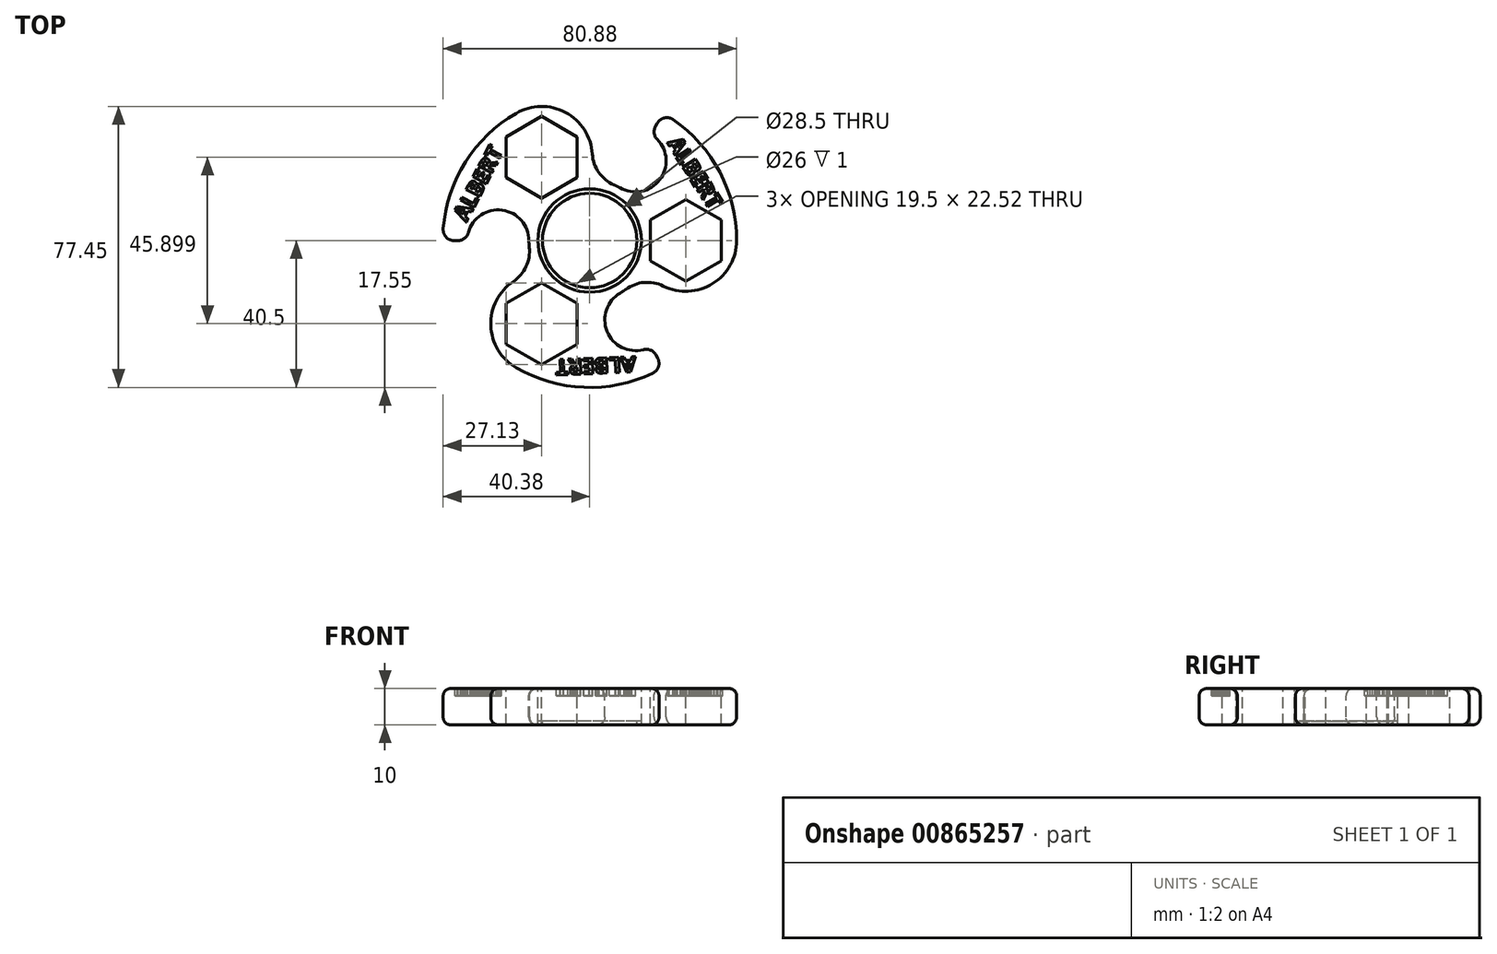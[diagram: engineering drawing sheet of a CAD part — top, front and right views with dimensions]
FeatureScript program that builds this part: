
annotation { "Feature Type Name" : "Feature", "Feature Type Description" : "" }
export const myFeature = defineFeature(function(context is Context, id is Id, definition is map)
    precondition{}
    {
        {
            var Q0;
            Q0=qCreatedBy(makeId("Top.planeOp"),FACE);
            var sketch = newSketch(context, id + "F0", { "sketchPlane" : qUnion([Q0])});
            skCircle(sketch, "E0", {"center": v(0, 0) * mm, "radius": 14.25 * mm});
            skCircle(sketch, "E1.cCircle", {"center": v(26.5, 0) * mm, "radius": 9.75 * mm, "construction": true});
            skLineSegment(sketch, "E1.0", {"start": v(36.25, 5.63) * mm, "end": v(36.25, -5.63) * mm});
            skLineSegment(sketch, "E1.1", {"start": v(36.25, -5.63) * mm, "end": v(26.5, -11.26) * mm});
            skLineSegment(sketch, "E1.2", {"start": v(26.5, -11.26) * mm, "end": v(16.75, -5.63) * mm});
            skLineSegment(sketch, "E1.3", {"start": v(16.75, -5.63) * mm, "end": v(16.75, 5.63) * mm});
            skLineSegment(sketch, "E1.4", {"start": v(16.75, 5.63) * mm, "end": v(26.5, 11.26) * mm});
            skLineSegment(sketch, "E1.5", {"start": v(26.5, 11.26) * mm, "end": v(36.25, 5.63) * mm});
            skPoint(sketch, "E1.0.midPoint", {"position": v(9.75, 0) * mm});
            skLineSegment(sketch, "E2", {"start": v(26.5, 11.26) * mm, "end": v(16.75, 5.63) * mm});
            skLineSegment(sketch, "E3", {"start": v(16.75, 5.63) * mm, "end": v(16.75, -5.63) * mm});
            skLineSegment(sketch, "E4", {"start": v(16.75, -5.63) * mm, "end": v(26.5, -11.26) * mm});
            skLineSegment(sketch, "E5", {"start": v(26.5, -11.26) * mm, "end": v(36.25, -5.63) * mm});
            skLineSegment(sketch, "E6", {"start": v(36.25, -5.63) * mm, "end": v(36.25, 5.63) * mm});
            skLineSegment(sketch, "E7", {"start": v(36.25, 5.63) * mm, "end": v(26.5, 11.26) * mm});
            skArc(sketch, "E8", {"start": v(8.38, 14.5) * mm, "mid": v(7.55, 14.95) * mm, "end": v(6.7, 15.35) * mm});
            skArc(sketch, "E9", {"start": v(20.3, -12.56) * mm, "mid": v(33.9, -11.89) * mm, "end": v(40.5, 0) * mm});
            skArc(sketch, "E10", {"start": v(40.5, 0) * mm, "mid": v(35.85, 18.84) * mm, "end": v(22.97, 33.35) * mm});
            skLineSegment(sketch, "E11", {"start": v(8.32, 14.54) * mm, "end": v(8.32, 14.54) * mm});
            skArc(sketch, "E12", {"start": v(8.32, 14.54) * mm, "mid": v(19.3, 16.7) * mm, "end": v(18.62, 27.87) * mm});
            skLineSegment(sketch, "E13.trimOffspring", {"start": v(18.16, 31.5) * mm, "end": v(18.68, 32.39) * mm});
            skPoint(sketch, "E14.visualSharp", {"position": v(14.85, -7.76) * mm});
            skArc(sketch, "E14.filletArc", {"start": v(20.3, -12.56) * mm, "mid": v(15, -11.56) * mm, "end": v(9.95, -13.48) * mm});
            skPoint(sketch, "E15.visualSharp", {"position": v(20.24, 35.08) * mm});
            skArc(sketch, "E15.filletArc", {"start": v(22.97, 33.35) * mm, "mid": v(20.62, 33.8) * mm, "end": v(18.68, 32.39) * mm});
            skPoint(sketch, "E16.visualSharp", {"position": v(16.85, 29.24) * mm});
            skArc(sketch, "E16.filletArc", {"start": v(18.16, 31.5) * mm, "mid": v(17.78, 29.6) * mm, "end": v(18.62, 27.87) * mm});
            skArc(sketch, "E17.1.0", {"start": v(-16.75, -0.07) * mm, "mid": v(-24.11, 8.38) * mm, "end": v(-33.45, 2.19) * mm});
            skArc(sketch, "E17.1.1", {"start": v(-36.35, -0.02) * mm, "mid": v(-34.53, 0.6) * mm, "end": v(-33.45, 2.19) * mm});
            skLineSegment(sketch, "E17.1.2", {"start": v(-36.35, -0.02) * mm, "end": v(-37.39, -0.02) * mm});
            skArc(sketch, "E17.1.3", {"start": v(-40.37, 3.22) * mm, "mid": v(-39.59, 0.95) * mm, "end": v(-37.39, -0.02) * mm});
            skArc(sketch, "E17.1.4", {"start": v(-20.25, 35.07) * mm, "mid": v(-34.24, 21.63) * mm, "end": v(-40.37, 3.22) * mm});
            skArc(sketch, "E17.1.5", {"start": v(0.72, 23.86) * mm, "mid": v(-6.65, 35.3) * mm, "end": v(-20.25, 35.07) * mm});
            skArc(sketch, "E17.1.6", {"start": v(0.72, 23.86) * mm, "mid": v(2.52, 18.77) * mm, "end": v(6.7, 15.35) * mm});
            skLineSegment(sketch, "E17.1.7", {"start": v(-3.5, 17.32) * mm, "end": v(-3.5, 28.58) * mm});
            skLineSegment(sketch, "E17.1.8", {"start": v(-3.5, 28.58) * mm, "end": v(-13.25, 34.2) * mm});
            skLineSegment(sketch, "E17.1.9", {"start": v(-13.25, 34.2) * mm, "end": v(-23, 28.58) * mm});
            skLineSegment(sketch, "E17.1.10", {"start": v(-23, 28.58) * mm, "end": v(-23, 17.32) * mm});
            skLineSegment(sketch, "E17.1.11", {"start": v(-23, 17.32) * mm, "end": v(-13.25, 11.7) * mm});
            skLineSegment(sketch, "E17.1.12", {"start": v(-13.25, 11.7) * mm, "end": v(-3.5, 17.32) * mm});
            skArc(sketch, "E17.2.0", {"start": v(8.43, -14.47) * mm, "mid": v(4.8, -25.07) * mm, "end": v(14.83, -30.06) * mm});
            skArc(sketch, "E17.2.1", {"start": v(18.2, -31.47) * mm, "mid": v(16.75, -30.2) * mm, "end": v(14.83, -30.06) * mm});
            skLineSegment(sketch, "E17.2.2", {"start": v(18.2, -31.47) * mm, "end": v(18.71, -32.37) * mm});
            skArc(sketch, "E17.2.3", {"start": v(17.4, -36.57) * mm, "mid": v(18.97, -34.76) * mm, "end": v(18.71, -32.37) * mm});
            skArc(sketch, "E17.2.4", {"start": v(-20.25, -35.07) * mm, "mid": v(-1.61, -40.47) * mm, "end": v(17.4, -36.57) * mm});
            skArc(sketch, "E17.2.5", {"start": v(-21.03, -11.3) * mm, "mid": v(-27.24, -23.4) * mm, "end": v(-20.25, -35.07) * mm});
            skArc(sketch, "E17.2.6", {"start": v(-21.03, -11.3) * mm, "mid": v(-17.51, -7.2) * mm, "end": v(-16.64, -1.87) * mm});
            skLineSegment(sketch, "E17.2.7", {"start": v(-13.25, -11.7) * mm, "end": v(-23, -17.32) * mm});
            skLineSegment(sketch, "E17.2.8", {"start": v(-23, -17.32) * mm, "end": v(-23, -28.58) * mm});
            skLineSegment(sketch, "E17.2.9", {"start": v(-23, -28.58) * mm, "end": v(-13.25, -34.2) * mm});
            skLineSegment(sketch, "E17.2.10", {"start": v(-13.25, -34.2) * mm, "end": v(-3.5, -28.58) * mm});
            skLineSegment(sketch, "E17.2.11", {"start": v(-3.5, -28.58) * mm, "end": v(-3.5, -17.32) * mm});
            skLineSegment(sketch, "E17.2.12", {"start": v(-3.5, -17.32) * mm, "end": v(-13.25, -11.7) * mm});
            skArc(sketch, "E18.trimOffspring", {"start": v(-16.75, 0) * mm, "mid": v(-16.72, -0.94) * mm, "end": v(-16.64, -1.87) * mm});
            skArc(sketch, "E19.trimOffspring", {"start": v(8.37, -14.5) * mm, "mid": v(9.17, -14.02) * mm, "end": v(9.95, -13.48) * mm});
            skSolve(sketch);
        }
        {
            var Q0;
            Q0=qCreatedBy(makeId("Top.planeOp"),FACE);
            cPlane(context, id + "F1", {"entities" : qUnion([Q0]), "cplaneType" : CPlaneType.OFFSET, "offset" : 5 * mm, "width" : 150 * mm, "height" : 150 * mm});
        }
        {
            var Q0;
            Q0=qCreatedBy(id+"F1.planeOp",FACE);
            var sketch = newSketch(context, id + "F2", { "sketchPlane" : qUnion([Q0])});
            skText(sketch, "E20", { "text": "ALBERT", "fontName": "OpenSans-Bold.ttf"});
            const initialGuessF2  = {"E20": [0.0214, 0.0269, 0.53415, -0.84539, 0.00426]};
            skSetInitialGuess(sketch, initialGuessF2);
            skSolve(sketch);
        }
        {
            var Q0;
            Q0=qCreatedBy(makeId("Top.planeOp"),FACE);
            var sketch = newSketch(context, id + "F3", { "sketchPlane" : qUnion([Q0])});
            skCircle(sketch, "E21", {"center": v(0, 0) * mm, "radius": 14.25 * mm});
            skCircle(sketch, "E22", {"center": v(0, 0) * mm, "radius": 13 * mm});
            skSolve(sketch);
        }
        {
            var Q0;
            Q0=makeQuery(id+"F0.imprint","IMPRINT",FACE,{"disambiguationData":[TD([[makeQuery(id+"F0.imprint","IMPRINT",EDGE,{"derivedFrom":sQuery(id+"F0.wireOp",EDGE,"E0")}),-1.0]])]});
            extrude(context, id + "F4", {"entities" : qUnion([Q0]), "depth" : -10 * mm, "offsetDistance" : 25 * mm});
        }
        {
            var Q0;
            Q0=makeQuery(id+"F3.imprint","IMPRINT",FACE,{"disambiguationData":[TD([[makeQuery(id+"F3.imprint","IMPRINT",EDGE,{"derivedFrom":sQuery(id+"F3.wireOp",EDGE,"E21")}),1.0]])]});
            extrude(context, id + "F5", {"entities" : qUnion([Q0]), "depth" : -1 * mm, "offsetDistance" : 25 * mm});
        }
        {
            var Q0;
            Q0 = qSketchRegion(id + "F2", true);
            extrude(context, id + "F6", {"entities" : qUnion([Q0]), "depth" : -7 * mm, "offsetDistance" : 25 * mm});
        }
        {
            var Q0;
            Q0=makeQuery(id+"F4.opExtrude","CAP_EDGE",EDGE,{"disambiguationData":[OSD([sQuery(id+"F0.wireOp",EDGE,"E17.1.4")])],"isStart":true});
            var Q1;
            Q1=makeQuery(id+"F4.opExtrude","CAP_EDGE",EDGE,{"disambiguationData":[OSD([sQuery(id+"F0.wireOp",EDGE,"E17.1.5")])],"isStart":true});
            var Q2;
            Q2=makeQuery(id+"F4.opExtrude","CAP_EDGE",EDGE,{"disambiguationData":[OSD([sQuery(id+"F0.wireOp",EDGE,"E12")])],"isStart":true});
            var Q3;
            Q3=makeQuery(id+"F4.opExtrude","CAP_EDGE",EDGE,{"disambiguationData":[OSD([sQuery(id+"F0.wireOp",EDGE,"E17.2.2")])],"isStart":true});
            fillet(context, id + "F7", {"entities" : qUnion([Q0, Q1, Q2, Q3]), "radius" : 2 * mm, "tangentPropagation" : true, "allowEdgeOverflow" : false});
        }
        {
            var Q0;
            Q0=makeQuery(id+"F4.opExtrude","CAP_EDGE",EDGE,{"disambiguationData":[OSD([sQuery(id+"F0.wireOp",EDGE,"E17.2.4")])],"isStart":false});
            var Q1;
            Q1=makeQuery(id+"F4.opExtrude","CAP_EDGE",EDGE,{"disambiguationData":[OSD([sQuery(id+"F0.wireOp",EDGE,"E17.2.3")])],"isStart":false});
            var Q2;
            Q2=makeQuery(id+"F4.opExtrude","CAP_EDGE",EDGE,{"disambiguationData":[OSD([sQuery(id+"F0.wireOp",EDGE,"E9")])],"isStart":false});
            var Q3;
            Q3=makeQuery(id+"F4.opExtrude","CAP_EDGE",EDGE,{"disambiguationData":[OSD([sQuery(id+"F0.wireOp",EDGE,"E17.1.5")])],"isStart":false});
            fillet(context, id + "F8", {"entities" : qUnion([Q0, Q1, Q2, Q3]), "radius" : 2.1 * mm, "tangentPropagation" : true, "allowEdgeOverflow" : false});
        }
        {
            var Q0;
            Q0=makeQuery(id+"F6.opExtrude","SWEPT_BODY",BODY,{"disambiguationData":[OSD([sQuery(id+"F2.wireOp",EDGE,"E20.sketch_text.stroke-74"),sQuery(id+"F2.wireOp",EDGE,"E20.sketch_text.stroke-75"),sQuery(id+"F2.wireOp",EDGE,"E20.sketch_text.stroke-76"),sQuery(id+"F2.wireOp",EDGE,"E20.sketch_text.stroke-77"),sQuery(id+"F2.wireOp",EDGE,"E20.sketch_text.stroke-78"),sQuery(id+"F2.wireOp",EDGE,"E20.sketch_text.stroke-79"),sQuery(id+"F2.wireOp",EDGE,"E20.sketch_text.stroke-80"),sQuery(id+"F2.wireOp",EDGE,"E20.sketch_text.stroke-81")])]});
            var Q1;
            Q1=makeQuery(id+"F6.opExtrude","SWEPT_BODY",BODY,{"disambiguationData":[OSD([sQuery(id+"F2.wireOp",EDGE,"E20.sketch_text.stroke-55"),sQuery(id+"F2.wireOp",EDGE,"E20.sketch_text.stroke-56"),sQuery(id+"F2.wireOp",EDGE,"E20.sketch_text.stroke-57"),sQuery(id+"F2.wireOp",EDGE,"E20.sketch_text.stroke-58"),sQuery(id+"F2.wireOp",EDGE,"E20.sketch_text.stroke-59"),sQuery(id+"F2.wireOp",EDGE,"E20.sketch_text.stroke-60"),sQuery(id+"F2.wireOp",EDGE,"E20.sketch_text.stroke-61"),sQuery(id+"F2.wireOp",EDGE,"E20.sketch_text.stroke-62"),sQuery(id+"F2.wireOp",EDGE,"E20.sketch_text.stroke-63"),sQuery(id+"F2.wireOp",EDGE,"E20.sketch_text.stroke-64"),sQuery(id+"F2.wireOp",EDGE,"E20.sketch_text.stroke-65"),sQuery(id+"F2.wireOp",EDGE,"E20.sketch_text.stroke-66"),sQuery(id+"F2.wireOp",EDGE,"E20.sketch_text.stroke-67"),sQuery(id+"F2.wireOp",EDGE,"E20.sketch_text.stroke-68"),sQuery(id+"F2.wireOp",EDGE,"E20.sketch_text.stroke-69"),sQuery(id+"F2.wireOp",EDGE,"E20.sketch_text.stroke-70"),sQuery(id+"F2.wireOp",EDGE,"E20.sketch_text.stroke-71"),sQuery(id+"F2.wireOp",EDGE,"E20.sketch_text.stroke-72"),sQuery(id+"F2.wireOp",EDGE,"E20.sketch_text.stroke-73")])]});
            var Q2;
            Q2=makeQuery(id+"F6.opExtrude","SWEPT_BODY",BODY,{"disambiguationData":[OSD([sQuery(id+"F2.wireOp",EDGE,"E20.sketch_text.stroke-43"),sQuery(id+"F2.wireOp",EDGE,"E20.sketch_text.stroke-44"),sQuery(id+"F2.wireOp",EDGE,"E20.sketch_text.stroke-45"),sQuery(id+"F2.wireOp",EDGE,"E20.sketch_text.stroke-46"),sQuery(id+"F2.wireOp",EDGE,"E20.sketch_text.stroke-47"),sQuery(id+"F2.wireOp",EDGE,"E20.sketch_text.stroke-48"),sQuery(id+"F2.wireOp",EDGE,"E20.sketch_text.stroke-49"),sQuery(id+"F2.wireOp",EDGE,"E20.sketch_text.stroke-50"),sQuery(id+"F2.wireOp",EDGE,"E20.sketch_text.stroke-51"),sQuery(id+"F2.wireOp",EDGE,"E20.sketch_text.stroke-52"),sQuery(id+"F2.wireOp",EDGE,"E20.sketch_text.stroke-53"),sQuery(id+"F2.wireOp",EDGE,"E20.sketch_text.stroke-54")])]});
            var Q3;
            Q3=makeQuery(id+"F6.opExtrude","SWEPT_BODY",BODY,{"disambiguationData":[OSD([sQuery(id+"F2.wireOp",EDGE,"E20.sketch_text.stroke-18"),sQuery(id+"F2.wireOp",EDGE,"E20.sketch_text.stroke-19"),sQuery(id+"F2.wireOp",EDGE,"E20.sketch_text.stroke-20"),sQuery(id+"F2.wireOp",EDGE,"E20.sketch_text.stroke-21"),sQuery(id+"F2.wireOp",EDGE,"E20.sketch_text.stroke-22"),sQuery(id+"F2.wireOp",EDGE,"E20.sketch_text.stroke-23"),sQuery(id+"F2.wireOp",EDGE,"E20.sketch_text.stroke-24"),sQuery(id+"F2.wireOp",EDGE,"E20.sketch_text.stroke-25"),sQuery(id+"F2.wireOp",EDGE,"E20.sketch_text.stroke-26"),sQuery(id+"F2.wireOp",EDGE,"E20.sketch_text.stroke-27"),sQuery(id+"F2.wireOp",EDGE,"E20.sketch_text.stroke-28"),sQuery(id+"F2.wireOp",EDGE,"E20.sketch_text.stroke-29"),sQuery(id+"F2.wireOp",EDGE,"E20.sketch_text.stroke-30"),sQuery(id+"F2.wireOp",EDGE,"E20.sketch_text.stroke-31"),sQuery(id+"F2.wireOp",EDGE,"E20.sketch_text.stroke-32"),sQuery(id+"F2.wireOp",EDGE,"E20.sketch_text.stroke-33"),sQuery(id+"F2.wireOp",EDGE,"E20.sketch_text.stroke-34"),sQuery(id+"F2.wireOp",EDGE,"E20.sketch_text.stroke-35"),sQuery(id+"F2.wireOp",EDGE,"E20.sketch_text.stroke-36"),sQuery(id+"F2.wireOp",EDGE,"E20.sketch_text.stroke-37"),sQuery(id+"F2.wireOp",EDGE,"E20.sketch_text.stroke-38"),sQuery(id+"F2.wireOp",EDGE,"E20.sketch_text.stroke-39"),sQuery(id+"F2.wireOp",EDGE,"E20.sketch_text.stroke-40"),sQuery(id+"F2.wireOp",EDGE,"E20.sketch_text.stroke-41"),sQuery(id+"F2.wireOp",EDGE,"E20.sketch_text.stroke-42")])]});
            var Q4;
            Q4=makeQuery(id+"F6.opExtrude","SWEPT_BODY",BODY,{"disambiguationData":[OSD([sQuery(id+"F2.wireOp",EDGE,"E20.sketch_text.stroke-0"),sQuery(id+"F2.wireOp",EDGE,"E20.sketch_text.stroke-1"),sQuery(id+"F2.wireOp",EDGE,"E20.sketch_text.stroke-2"),sQuery(id+"F2.wireOp",EDGE,"E20.sketch_text.stroke-3"),sQuery(id+"F2.wireOp",EDGE,"E20.sketch_text.stroke-4"),sQuery(id+"F2.wireOp",EDGE,"E20.sketch_text.stroke-5"),sQuery(id+"F2.wireOp",EDGE,"E20.sketch_text.stroke-6"),sQuery(id+"F2.wireOp",EDGE,"E20.sketch_text.stroke-7"),sQuery(id+"F2.wireOp",EDGE,"E20.sketch_text.stroke-8"),sQuery(id+"F2.wireOp",EDGE,"E20.sketch_text.stroke-9"),sQuery(id+"F2.wireOp",EDGE,"E20.sketch_text.stroke-10"),sQuery(id+"F2.wireOp",EDGE,"E20.sketch_text.stroke-11")])]});
            var Q5;
            Q5=makeQuery(id+"F6.opExtrude","SWEPT_BODY",BODY,{"disambiguationData":[OSD([sQuery(id+"F2.wireOp",EDGE,"E20.sketch_text.stroke-12"),sQuery(id+"F2.wireOp",EDGE,"E20.sketch_text.stroke-13"),sQuery(id+"F2.wireOp",EDGE,"E20.sketch_text.stroke-14"),sQuery(id+"F2.wireOp",EDGE,"E20.sketch_text.stroke-15"),sQuery(id+"F2.wireOp",EDGE,"E20.sketch_text.stroke-16"),sQuery(id+"F2.wireOp",EDGE,"E20.sketch_text.stroke-17")])]});
            var Q6;
            Q6=makeQuery(id+"F5.opExtrude","CAP_EDGE",EDGE,{"disambiguationData":[OSD([sQuery(id+"F3.wireOp",EDGE,"E22")])],"isStart":false});
            circularPattern(context, id + "F9", {"operationType" : NewBodyOperationType.REMOVE, "entities" : qUnion([Q0, Q1, Q2, Q3, Q4, Q5]), "axis" : qUnion([Q6]), "angle" : 360 * degree, "instanceCount" : 3, "equalSpace" : true, "computeTransformsWithoutBuiltin" : true});
        }
        {
            var Q0;
            Q0=makeQuery(id+"F5.opExtrude","SWEPT_BODY",BODY,{"disambiguationData":[OSD([sQuery(id+"F3.wireOp",EDGE,"E21"),sQuery(id+"F3.wireOp",EDGE,"E22")])]});
            transform(context, id + "F10", {"entities" : qUnion([Q0]), "transformType" : TransformType.TRANSLATION_3D, "dx" : 0 * mm, "dy" : 0 * mm, "dz" : -9 * mm, "makeCopy" : false});
        }
    });
